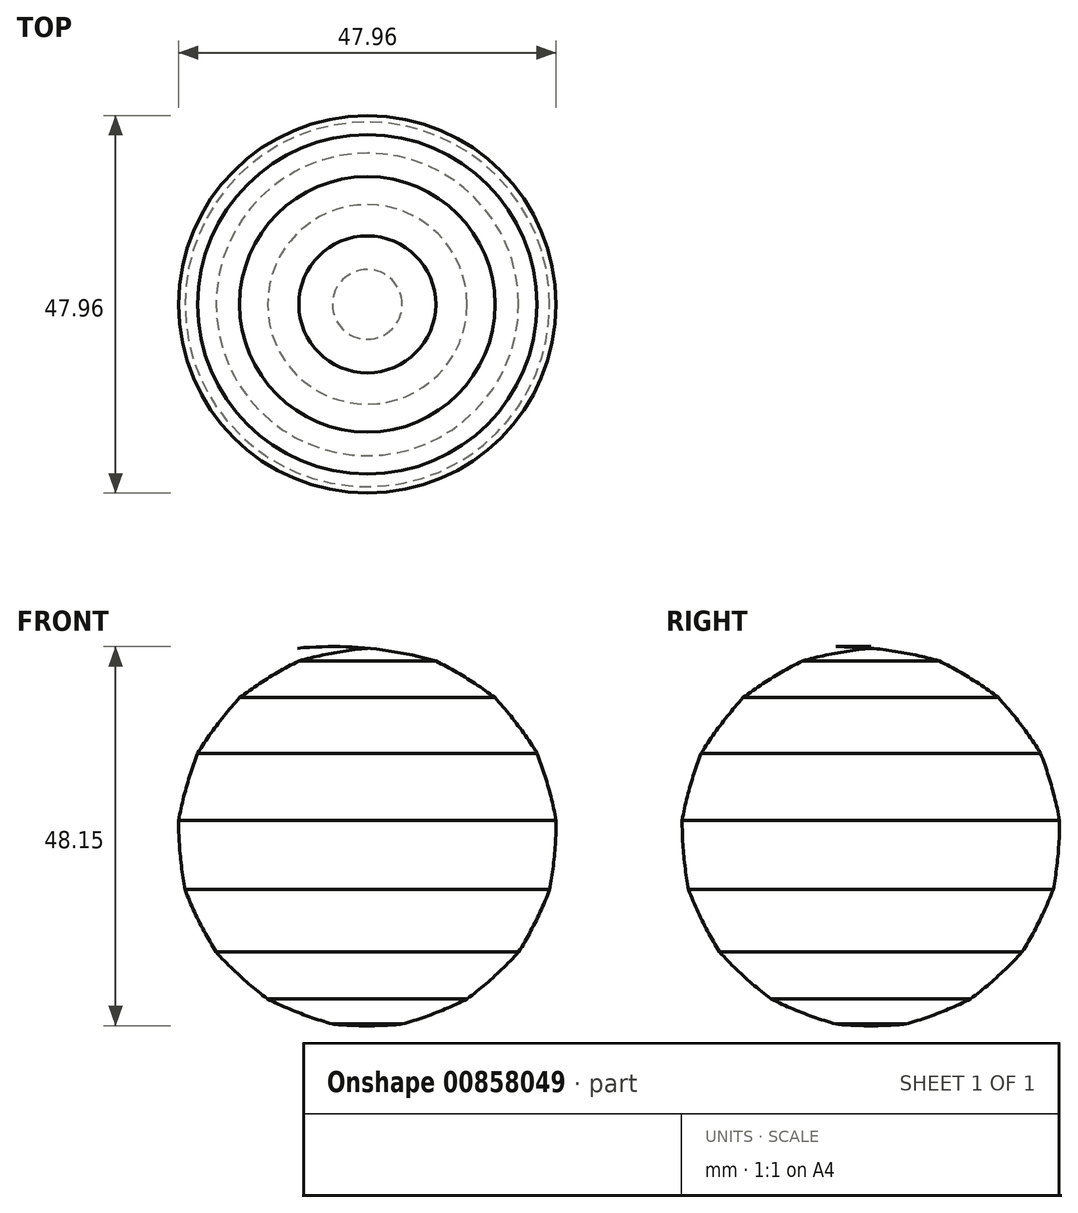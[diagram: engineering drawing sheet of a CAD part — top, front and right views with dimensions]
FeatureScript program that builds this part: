
annotation { "Feature Type Name" : "Feature", "Feature Type Description" : "" }
export const myFeature = defineFeature(function(context is Context, id is Id, definition is map)
    precondition{}
    {
        {
            var Q0;
            Q0=qCreatedBy(makeId("Front.planeOp"),FACE);
            var sketch = newSketch(context, id + "F0", { "sketchPlane" : qUnion([Q0])});
            skPoint(sketch, "E0.0.midPoint", {"position": v(0, -23.87) * mm});
            skCircle(sketch, "E1", {"center": v(0, 24.08) * mm, "radius": 47.95 * mm});
            skCircle(sketch, "E2", {"center": v(8.7, 22.45) * mm, "radius": 47.95 * mm});
            skCircle(sketch, "E3", {"center": v(16.22, 17.8) * mm, "radius": 47.95 * mm});
            skCircle(sketch, "E4", {"center": v(21.55, 10.73) * mm, "radius": 47.95 * mm});
            skCircle(sketch, "E5", {"center": v(23.98, 2.22) * mm, "radius": 47.95 * mm});
            skCircle(sketch, "E6", {"center": v(23.16, -6.59) * mm, "radius": 47.95 * mm});
            skCircle(sketch, "E7", {"center": v(19.22, -14.51) * mm, "radius": 47.95 * mm});
            skCircle(sketch, "E8", {"center": v(12.68, -20.47) * mm, "radius": 47.95 * mm});
            skCircle(sketch, "E9", {"center": v(4.42, -23.67) * mm, "radius": 47.95 * mm});
            skCircle(sketch, "E10", {"center": v(-4.42, -23.67) * mm, "radius": 47.95 * mm});
            skCircle(sketch, "E11", {"center": v(-12.68, -20.47) * mm, "radius": 47.95 * mm});
            skCircle(sketch, "E12", {"center": v(-19.22, -14.51) * mm, "radius": 47.95 * mm});
            skCircle(sketch, "E13", {"center": v(-23.16, -6.59) * mm, "radius": 47.95 * mm});
            skCircle(sketch, "E14", {"center": v(-23.98, 2.22) * mm, "radius": 47.95 * mm});
            skCircle(sketch, "E15", {"center": v(-21.55, 10.73) * mm, "radius": 47.95 * mm});
            skCircle(sketch, "E16", {"center": v(-16.22, 17.8) * mm, "radius": 47.95 * mm});
            skCircle(sketch, "E17", {"center": v(-8.7, 22.45) * mm, "radius": 47.95 * mm});
            skLineSegment(sketch, "E18", {"start": v(0, -23.87) * mm, "end": v(0, 24.08) * mm});
            skSolve(sketch);
        }
        {
            var Q0;
            {var subQ5=sQuery(id+"F0.wireOp",EDGE,"E18");Q0=makeQuery(id+"F0.imprint","IMPRINT",FACE,{"disambiguationData":[TD([[makeQuery(id+"F0.imprint","IMPRINT",EDGE,{"derivedFrom":subQ5}),-1.0]])]});}
            var Q1;
            Q1=sQuery(id+"F0.wireOp",EDGE,"E18");
            revolve(context, id + "F1", {"surfaceOperationType" : NewSurfaceOperationType.NEW, "entities" : qUnion([Q0]), "axis" : qUnion([Q1]), "revolveType" : RevolveType.FULL});
        }
    });
